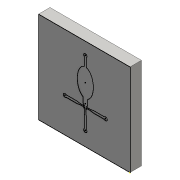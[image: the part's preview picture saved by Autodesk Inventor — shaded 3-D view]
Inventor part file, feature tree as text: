
AUTODESK INVENTOR PART (.ipt)
format: ipt  version: 2016 (Build 200138000, 138)  size: 141,824 bytes
history: native  units: mm
features: extrude x3, sketch x2, other x1
ambient origin geometry x8: Origin, YZ Plane, XZ Plane, XY Plane, X Axis, Y Axis, Z Axis, Center Point
bodies: Body1 (feature_tree)
feature tree (6):
  other  "Sólido1"
  sketch  "Boceto1"  dims[d7=5.0mm d8=0.0mm d9=0.2mm d10=0.0mm]
  extrude  "Extrusión1"  Depth=0.2mm TaperAngle=0.0deg
  extrude  "Extrusión2"  Depth=0.2mm
  extrude  "Extrusión3"  Depth=0.2mm
  sketch  "Boceto2"  dims[d11=0.7mm d12=0.7mm d13=0.7mm d14=0.7mm d15=0.2mm d16=0.0mm]
